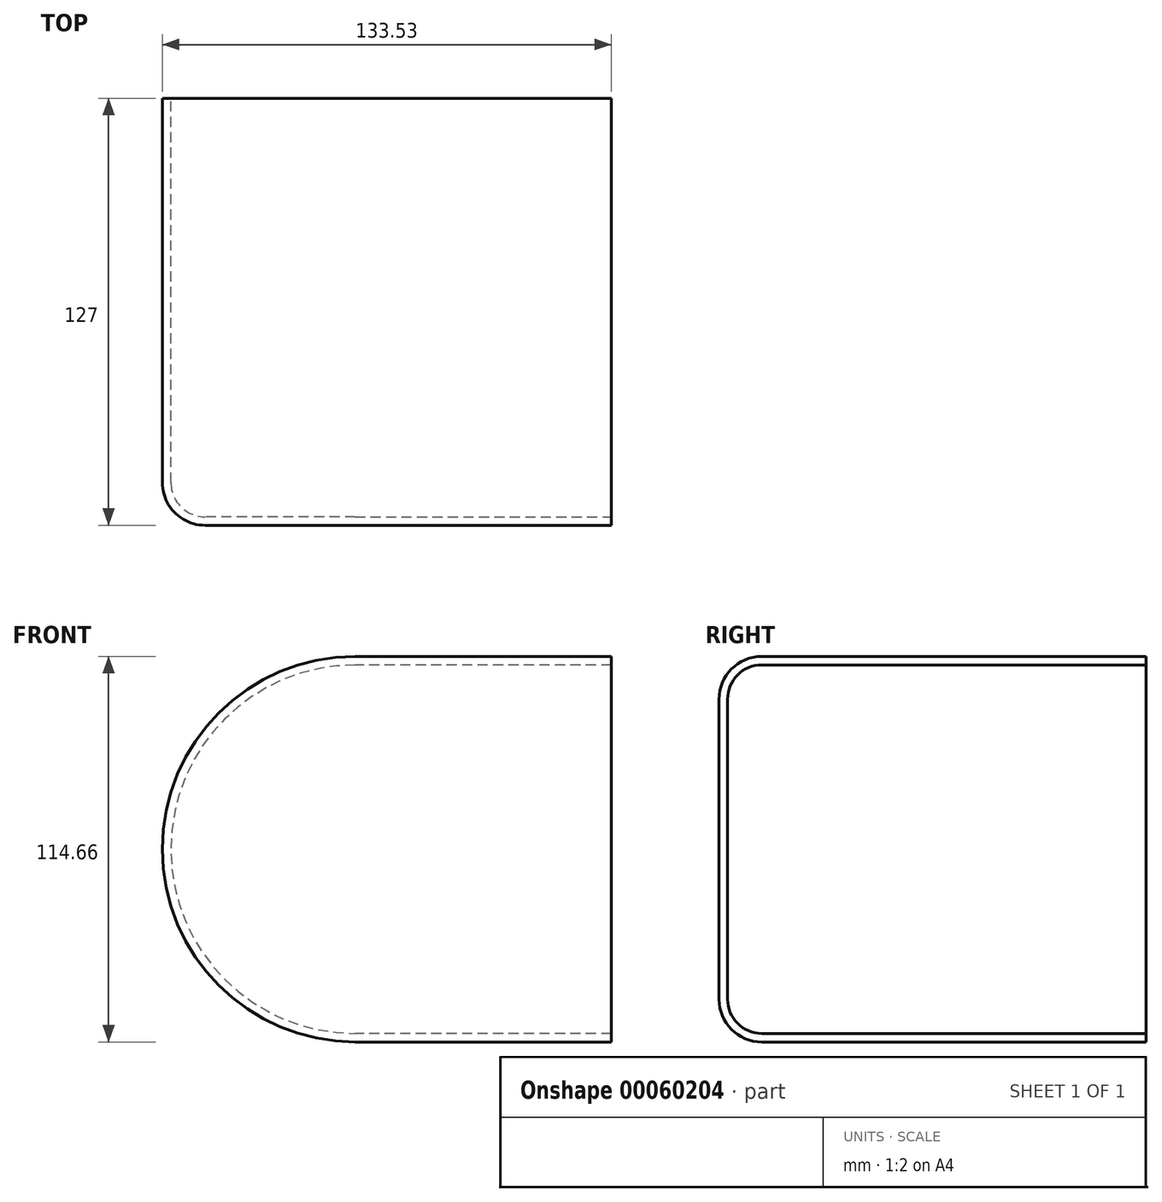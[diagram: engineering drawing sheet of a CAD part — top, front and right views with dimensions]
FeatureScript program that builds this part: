
annotation { "Feature Type Name" : "Feature", "Feature Type Description" : "" }
export const myFeature = defineFeature(function(context is Context, id is Id, definition is map)
    precondition{}
    {
        {
            var Q0;
            Q0=qCreatedBy(makeId("Front.planeOp"),FACE);
            var sketch = newSketch(context, id + "F0", { "sketchPlane" : qUnion([Q0])});
            skLineSegment(sketch, "E0.rect.bottom", {"start": v(38.1, 57.33) * mm, "end": v(-38.1, 57.33) * mm});
            skLineSegment(sketch, "E0.rect.top", {"start": v(38.1, -57.33) * mm, "end": v(-38.1, -57.33) * mm});
            skLineSegment(sketch, "E0.rect.left", {"start": v(38.1, 57.33) * mm, "end": v(38.1, -57.33) * mm});
            skLineSegment(sketch, "E0.rect.right", {"start": v(-38.1, 57.33) * mm, "end": v(-38.1, -57.33) * mm});
            skPoint(sketch, "E0.rect.middle", {"position": v(0, 0) * mm});
            skArc(sketch, "E1", {"start": v(-38.1, 57.33) * mm, "mid": v(-95.43, 0) * mm, "end": v(-38.1, -57.33) * mm});
            skSolve(sketch);
        }
        {
            var Q0;
            Q0=makeQuery(id+"F0.imprint","IMPRINT",FACE,{"disambiguationData":[TD([[makeQuery(id+"F0.imprint","IMPRINT",EDGE,{"derivedFrom":sQuery(id+"F0.wireOp",EDGE,"E0.rect.right")}),-1.0]])]});
            var Q1;
            Q1=makeQuery(id+"F0.imprint","IMPRINT",FACE,{"disambiguationData":[TD([[makeQuery(id+"F0.imprint","IMPRINT",EDGE,{"derivedFrom":sQuery(id+"F0.wireOp",EDGE,"E0.rect.bottom")}),1.0]])]});
            extrude(context, id + "F2", {"entities" : qUnion([Q0, Q1]), "depth" : 127 * mm});
        }
        {
            var Q0;
            Q0=makeQuery(id+"F2.opExtrude","CAP_EDGE",EDGE,{"disambiguationData":[OSD([sQuery(id+"F0.wireOp",EDGE,"E1")])],"isStart":false});
            fillet(context, id + "F3", {"entities" : qUnion([Q0]), "radius" : 12.7 * mm, "tangentPropagation" : true, "allowEdgeOverflow" : false});
        }
        {
            var Q0;
            Q0=makeQuery(id+"F2.opExtrude","SWEPT_FACE",FACE,{"disambiguationData":[OSD([sQuery(id+"F0.wireOp",EDGE,"E0.rect.left")])]});
            var Q1;
            Q1=makeQuery(id+"F2.opExtrude","CAP_FACE",FACE,{"disambiguationData":[OSD([sQuery(id+"F0.wireOp",EDGE,"E0.rect.bottom"),sQuery(id+"F0.wireOp",EDGE,"E0.rect.top"),sQuery(id+"F0.wireOp",EDGE,"E0.rect.left"),sQuery(id+"F0.wireOp",EDGE,"E1")])],"isStart":true});
            shell(context, id + "F1", {"entities" : qUnion([Q0, Q1]), "thickness" : 2.54 * mm});
        }
    });
